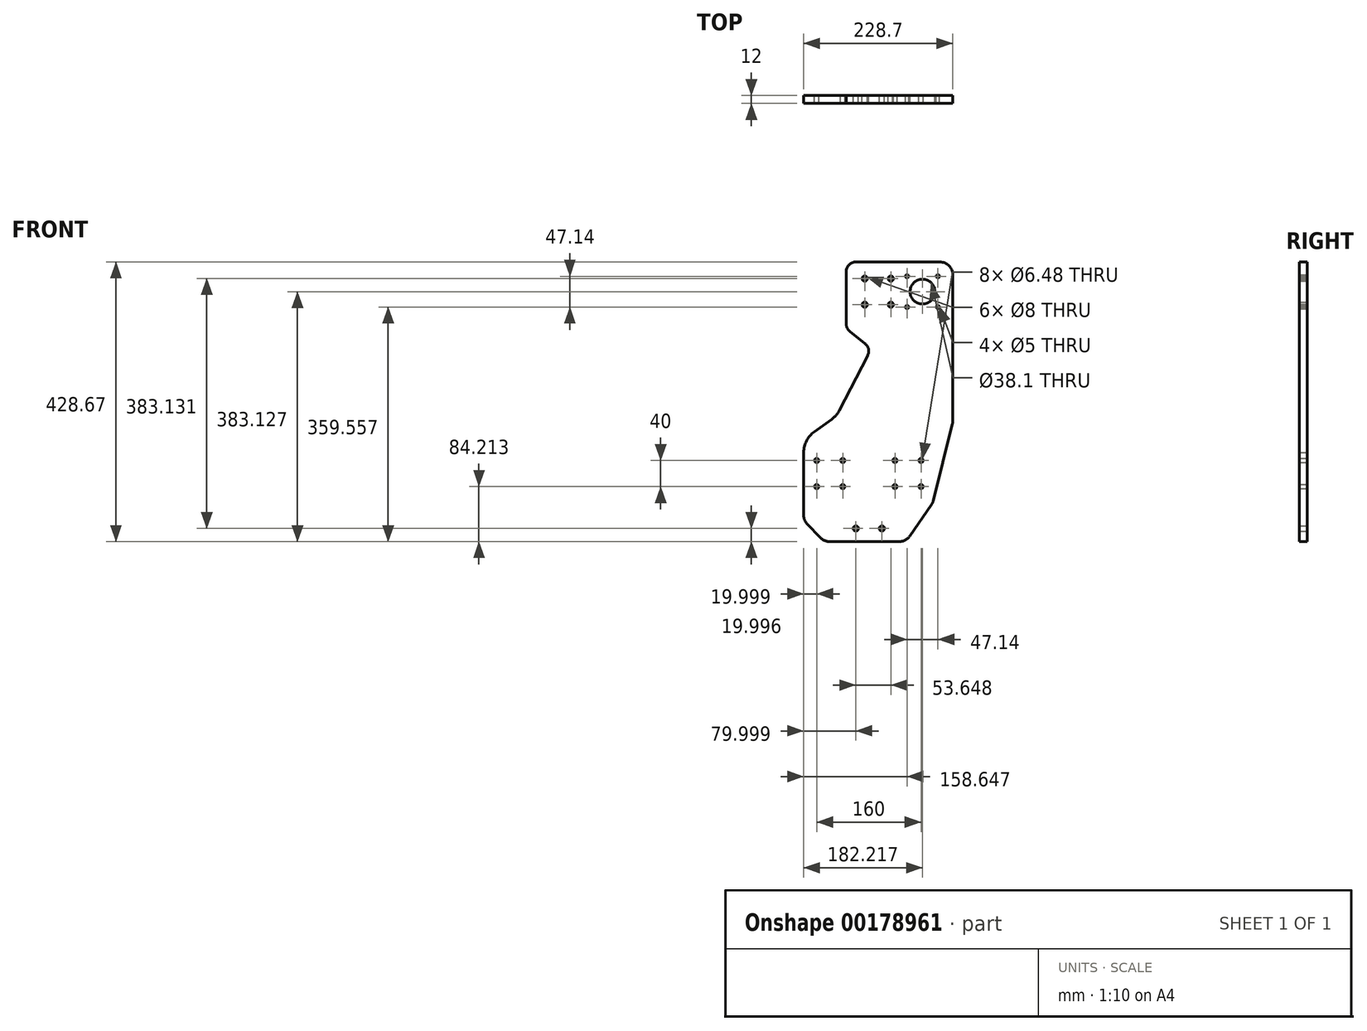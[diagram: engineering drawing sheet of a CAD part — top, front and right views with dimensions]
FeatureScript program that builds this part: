
annotation { "Feature Type Name" : "Feature", "Feature Type Description" : "" }
export const myFeature = defineFeature(function(context is Context, id is Id, definition is map)
    precondition{}
    {
        {
            var Q0;
            Q0=qCreatedBy(makeId("Front.planeOp"),FACE);
            var sketch = newSketch(context, id + "F0", { "sketchPlane" : qUnion([Q0])});
            skLineSegment(sketch, "E0.top", {"start": v(85.23, 205) * mm, "end": v(25.3, 205) * mm});
            skPoint(sketch, "E0.middle", {"position": v(0, 0) * mm});
            skLineSegment(sketch, "E1", {"start": v(135.36, -38.58) * mm, "end": v(135.36, 185) * mm});
            skLineSegment(sketch, "E2", {"start": v(115.36, 205) * mm, "end": v(85.23, 205) * mm});
            skLineSegment(sketch, "E3", {"start": v(-50.18, -36.07) * mm, "end": v(-76.73, -55.2) * mm});
            skCircle(sketch, "E4", {"center": v(-73.34, -139.46) * mm, "radius": 3.24 * mm});
            skCircle(sketch, "E5", {"center": v(-73.34, -99.46) * mm, "radius": 3.24 * mm});
            skCircle(sketch, "E6", {"center": v(-33.34, -99.46) * mm, "radius": 3.24 * mm});
            skCircle(sketch, "E7", {"center": v(-33.34, -139.46) * mm, "radius": 3.24 * mm});
            skCircle(sketch, "E8", {"center": v(46.66, -99.46) * mm, "radius": 3.24 * mm});
            skCircle(sketch, "E9", {"center": v(46.66, -139.46) * mm, "radius": 3.24 * mm});
            skCircle(sketch, "E10", {"center": v(86.66, -139.46) * mm, "radius": 3.24 * mm});
            skCircle(sketch, "E11", {"center": v(86.66, -99.46) * mm, "radius": 3.24 * mm});
            skCircle(sketch, "E12", {"center": v(-13.34, -203.67) * mm, "radius": 4 * mm});
            skCircle(sketch, "E13", {"center": v(26.66, -203.67) * mm, "radius": 4 * mm});
            skPoint(sketch, "E14.orphan", {"position": v(-84.77, 205) * mm});
            skPoint(sketch, "E15.visualSharp", {"position": v(-92.99, -66.91) * mm});
            skArc(sketch, "E15.filletArc", {"start": v(-76.73, -55.2) * mm, "mid": v(-88.79, -69.1) * mm, "end": v(-93.34, -86.95) * mm});
            skCircle(sketch, "E16", {"center": v(0.3, 179.46) * mm, "radius": 4 * mm});
            skCircle(sketch, "E17", {"center": v(40.3, 179.46) * mm, "radius": 4 * mm});
            skCircle(sketch, "E18", {"center": v(0.3, 139.46) * mm, "radius": 4 * mm});
            skCircle(sketch, "E19", {"center": v(40.3, 139.46) * mm, "radius": 4 * mm});
            skCircle(sketch, "E20", {"center": v(65.3, 183.03) * mm, "radius": 2.5 * mm});
            skCircle(sketch, "E21", {"center": v(112.45, 183.03) * mm, "radius": 2.5 * mm});
            skCircle(sketch, "E22", {"center": v(65.3, 135.89) * mm, "radius": 2.5 * mm});
            skCircle(sketch, "E23", {"center": v(112.45, 135.89) * mm, "radius": 2.5 * mm});
            skCircle(sketch, "E24", {"center": v(88.88, 159.46) * mm, "radius": 19.05 * mm});
            skPoint(sketch, "E25.visualSharp", {"position": v(135.36, 205) * mm});
            skArc(sketch, "E25.filletArc", {"start": v(135.36, 185) * mm, "mid": v(129.5, 199.14) * mm, "end": v(115.36, 205) * mm});
            skPoint(sketch, "E26.orphan", {"position": v(-34.7, 179.46) * mm});
            skPoint(sketch, "E27.visualSharp", {"position": v(-22, 205) * mm});
            skPoint(sketch, "E28.orphan", {"position": v(-34.7, 139.46) * mm});
            skPoint(sketch, "E29.orphan", {"position": v(135.36, 128.58) * mm});
            skLineSegment(sketch, "E30", {"start": v(25.3, 205) * mm, "end": v(25.3, 205) * mm});
            skLineSegment(sketch, "E31", {"start": v(25.3, 205) * mm, "end": v(10.35, 205) * mm});
            skPoint(sketch, "E32.visualSharp", {"position": v(0.04, 128.58) * mm});
            skPoint(sketch, "E33.orphan", {"position": v(47.2, 128.58) * mm});
            skLineSegment(sketch, "E34", {"start": v(42.47, 120.22) * mm, "end": v(42.47, 120.22) * mm});
            skLineSegment(sketch, "E35", {"start": v(0.04, 128.58) * mm, "end": v(-2.03, 128.58) * mm});
            skPoint(sketch, "E36.visualSharp", {"position": v(-11.41, 128.58) * mm});
            skLineSegment(sketch, "E37", {"start": v(-93.34, -86.95) * mm, "end": v(-93.34, -135.08) * mm});
            skPoint(sketch, "E38.visualSharp", {"position": v(-43.06, -30.95) * mm});
            skArc(sketch, "E38.filletArc", {"start": v(-50.18, -36.07) * mm, "mid": v(-43.91, -30.47) * mm, "end": v(-38.96, -23.69) * mm});
            skPoint(sketch, "E39.end.orphan", {"position": v(-14.64, 179.46) * mm});
            skLineSegment(sketch, "E40", {"start": v(3.97, 59.83) * mm, "end": v(-38.6, -23.02) * mm});
            skPoint(sketch, "E41.visualSharp", {"position": v(-35.75, 205) * mm});
            skPoint(sketch, "E42.visualSharp", {"position": v(-35.75, 100.23) * mm});
            skPoint(sketch, "E43.visualSharp", {"position": v(10.35, 72.27) * mm});
            skPoint(sketch, "E44.visualSharp", {"position": v(-38.75, -23.32) * mm});
            skArc(sketch, "E44.filletArc", {"start": v(-38.96, -23.69) * mm, "mid": v(-38.77, -23.36) * mm, "end": v(-38.6, -23.02) * mm});
            skLineSegment(sketch, "E45", {"start": v(10.35, 205) * mm, "end": v(-13, 205) * mm});
            skLineSegment(sketch, "E46", {"start": v(-28, 190) * mm, "end": v(-28, 109.95) * mm});
            skLineSegment(sketch, "E47", {"start": v(-22.33, 98.2) * mm, "end": v(0.71, 79.92) * mm});
            skLineSegment(sketch, "E48", {"start": v(4.73, 61.31) * mm, "end": v(3.97, 59.83) * mm});
            skPoint(sketch, "E49.visualSharp", {"position": v(-28, 205) * mm});
            skArc(sketch, "E49.filletArc", {"start": v(-13, 205) * mm, "mid": v(-23.61, 200.6) * mm, "end": v(-28, 190) * mm});
            skPoint(sketch, "E50.visualSharp", {"position": v(-28, 102.7) * mm});
            skArc(sketch, "E50.filletArc", {"start": v(-28, 109.95) * mm, "mid": v(-26.51, 103.43) * mm, "end": v(-22.33, 98.2) * mm});
            skArc(sketch, "E51.filletArc", {"start": v(4.73, 61.31) * mm, "mid": v(6.05, 71.33) * mm, "end": v(0.71, 79.92) * mm});
            skLineSegment(sketch, "E52", {"start": v(-93.34, -135.08) * mm, "end": v(-93.34, -183.04) * mm});
            skLineSegment(sketch, "E53", {"start": v(-53.7, -223.67) * mm, "end": v(53.23, -223.67) * mm});
            skLineSegment(sketch, "E54", {"start": v(105.34, -161.24) * mm, "end": v(134.76, -43.42) * mm});
            skLineSegment(sketch, "E55", {"start": v(-87.83, -196.83) * mm, "end": v(-68.18, -217.46) * mm});
            skPoint(sketch, "E56.orphan", {"position": v(-93.34, -223.67) * mm});
            skPoint(sketch, "E57.visualSharp", {"position": v(-93.34, -191.04) * mm});
            skArc(sketch, "E57.filletArc", {"start": v(-93.34, -183.04) * mm, "mid": v(-91.91, -190.47) * mm, "end": v(-87.83, -196.83) * mm});
            skPoint(sketch, "E58.visualSharp", {"position": v(-62.27, -223.67) * mm});
            skArc(sketch, "E58.filletArc", {"start": v(-68.18, -217.46) * mm, "mid": v(-61.58, -222.06) * mm, "end": v(-53.7, -223.67) * mm});
            skLineSegment(sketch, "E59", {"start": v(69.67, -215.05) * mm, "end": v(102.39, -167.77) * mm});
            skPoint(sketch, "E60.orphan", {"position": v(89.75, -223.67) * mm});
            skPoint(sketch, "E61.visualSharp", {"position": v(63.7, -223.67) * mm});
            skArc(sketch, "E61.filletArc", {"start": v(53.23, -223.67) * mm, "mid": v(62.51, -221.39) * mm, "end": v(69.67, -215.05) * mm});
            skPoint(sketch, "E62.visualSharp", {"position": v(104.46, -164.78) * mm});
            skArc(sketch, "E62.filletArc", {"start": v(102.39, -167.77) * mm, "mid": v(104.16, -164.64) * mm, "end": v(105.34, -161.24) * mm});
            skPoint(sketch, "E63.visualSharp", {"position": v(135.36, -41.04) * mm});
            skArc(sketch, "E63.filletArc", {"start": v(134.76, -43.42) * mm, "mid": v(135.21, -41.02) * mm, "end": v(135.36, -38.58) * mm});
            skSolve(sketch);
        }
        {
            var Q0;
            Q0=makeQuery(id+"F0.imprint","IMPRINT",FACE,{"disambiguationData":[TD([[makeQuery(id+"F0.imprint","IMPRINT",EDGE,{"derivedFrom":sQuery(id+"F0.wireOp",EDGE,"E0.top")}),1.0]])]});
            extrude(context, id + "F1", {"entities" : qUnion([Q0]), "depth" : 12 * mm});
        }
    });
